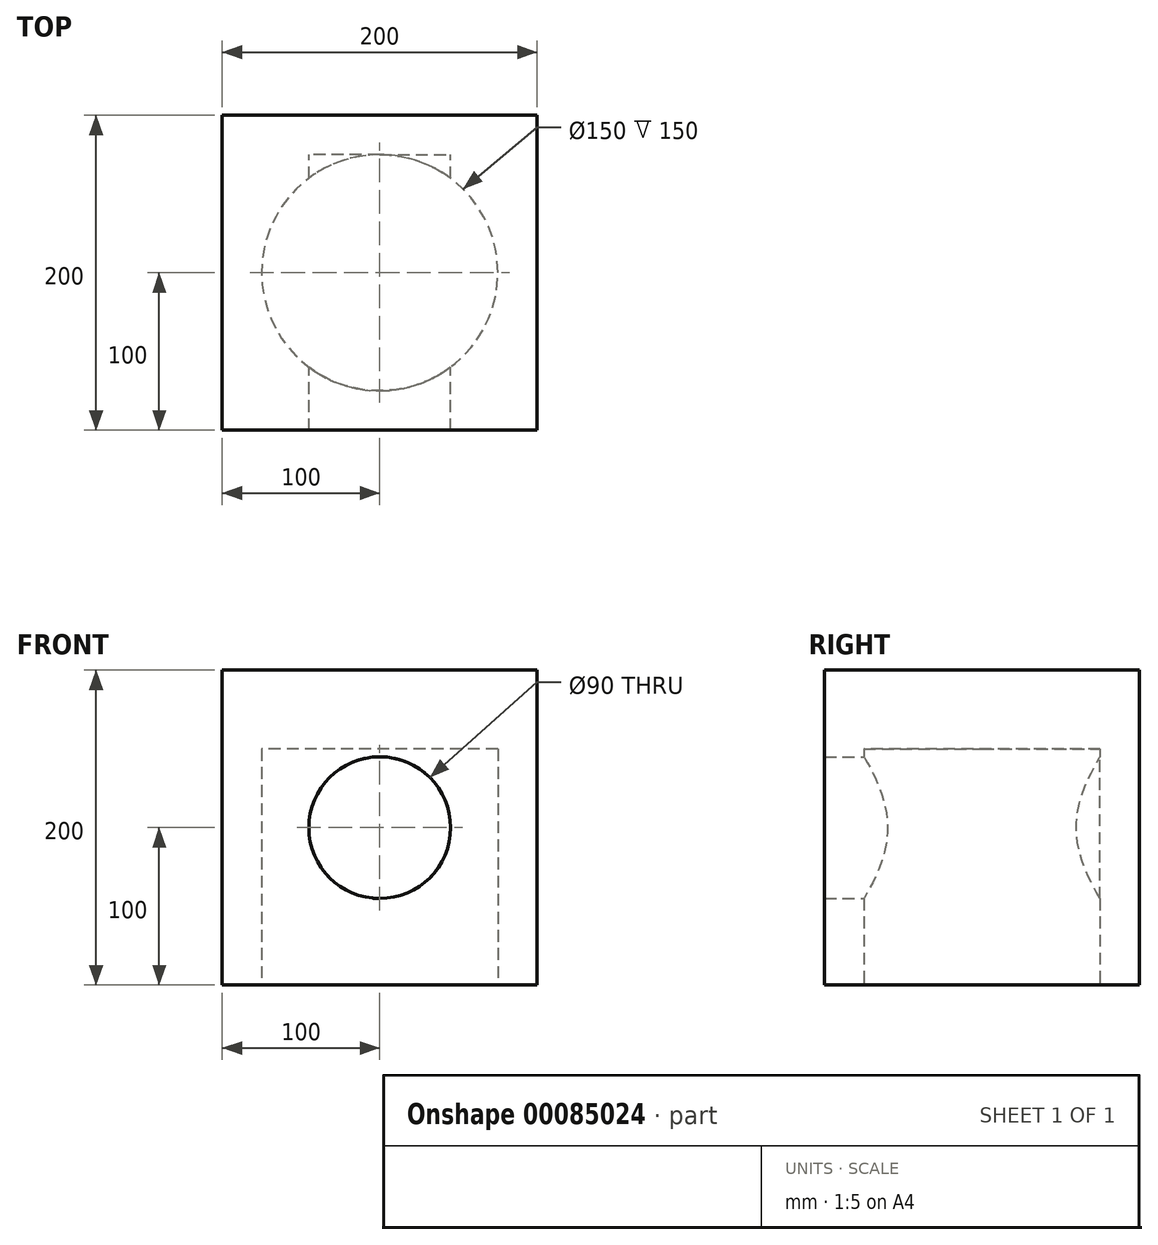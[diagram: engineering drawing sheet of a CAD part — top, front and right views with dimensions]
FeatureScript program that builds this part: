
annotation { "Feature Type Name" : "Feature", "Feature Type Description" : "" }
export const myFeature = defineFeature(function(context is Context, id is Id, definition is map)
    precondition{}
    {
        {
            var Q0;
            Q0=qCreatedBy(makeId("Front.planeOp"),FACE);
            var sketch = newSketch(context, id + "F0", { "sketchPlane" : qUnion([Q0])});
            skLineSegment(sketch, "E0", {"start": v(0, 0) * mm, "end": v(0, 200) * mm});
            skLineSegment(sketch, "E1", {"start": v(0, 200) * mm, "end": v(200, 200) * mm});
            skLineSegment(sketch, "E2", {"start": v(200, 200) * mm, "end": v(200, 0) * mm});
            skLineSegment(sketch, "E3", {"start": v(200, 0) * mm, "end": v(0, 0) * mm});
            skCircle(sketch, "E4", {"center": v(100, 100) * mm, "radius": 45 * mm});
            skLineSegment(sketch, "E5", {"start": v(100, 100) * mm, "end": v(100, 145) * mm});
            skSolve(sketch);
        }
        {
            var Q0;
            Q0=qSketchRegion(id+"F0",true);
            extrude(context, id + "F1", {"entities" : qUnion([Q0]), "depth" : 200 * mm});
        }
        {
            var Q0;
            Q0=qCreatedBy(makeId("Top.planeOp"),FACE);
            var sketch = newSketch(context, id + "F2", { "sketchPlane" : qUnion([Q0])});
            skLineSegment(sketch, "E6.bottom", {"start": v(0, 0) * mm, "end": v(200, 0) * mm});
            skLineSegment(sketch, "E6.top", {"start": v(0, -200) * mm, "end": v(200, -200) * mm});
            skLineSegment(sketch, "E6.left", {"start": v(0, 0) * mm, "end": v(0, -200) * mm});
            skLineSegment(sketch, "E6.right", {"start": v(200, 0) * mm, "end": v(200, -200) * mm});
            skCircle(sketch, "E7", {"center": v(100, -100) * mm, "radius": 75 * mm});
            skLineSegment(sketch, "E8", {"start": v(100, -100) * mm, "end": v(100, -175) * mm});
            skSolve(sketch);
        }
        {
            var Q0;
            Q0=makeQuery(id+"F2.imprint","IMPRINT",FACE,{"disambiguationData":[TD([[makeQuery(id+"F2.imprint","IMPRINT",EDGE,{"derivedFrom":sQuery(id+"F2.wireOp",EDGE,"E7")}),1.0]])]});
            extrude(context, id + "F3", {"entities" : qUnion([Q0]), "operationType" : NewBodyOperationType.REMOVE, "depth" : 150 * mm});
        }
        {
            var Q0;
            Q0=makeQuery(id+"F0.imprint","IMPRINT",FACE,{"disambiguationData":[TD([[makeQuery(id+"F0.imprint","IMPRINT",EDGE,{"derivedFrom":sQuery(id+"F0.wireOp",EDGE,"E4")}),1.0]])]});
            var Q1;
            Q1=makeQuery(id+"F1.opExtrude","SWEPT_FACE",FACE,{"disambiguationData":[OSD([sQuery(id+"F0.wireOp",EDGE,"E4")])]});
            var Q2;
            Q2=makeQuery(id+"F1.opExtrude","SWEPT_BODY",BODY,{"disambiguationData":[OSD([sQuery(id+"F0.wireOp",EDGE,"E0"),sQuery(id+"F0.wireOp",EDGE,"E1"),sQuery(id+"F0.wireOp",EDGE,"E2"),sQuery(id+"F0.wireOp",EDGE,"E3"),sQuery(id+"F0.wireOp",EDGE,"E4")])]});
            extrude(context, id + "F4", {"entities" : qUnion([Q0]), "operationType" : NewBodyOperationType.ADD, "endBoundEntityFace" : qUnion([Q1]), "endBoundEntityBody" : qUnion([Q2]), "depth" : 25 * mm});
        }
    });
